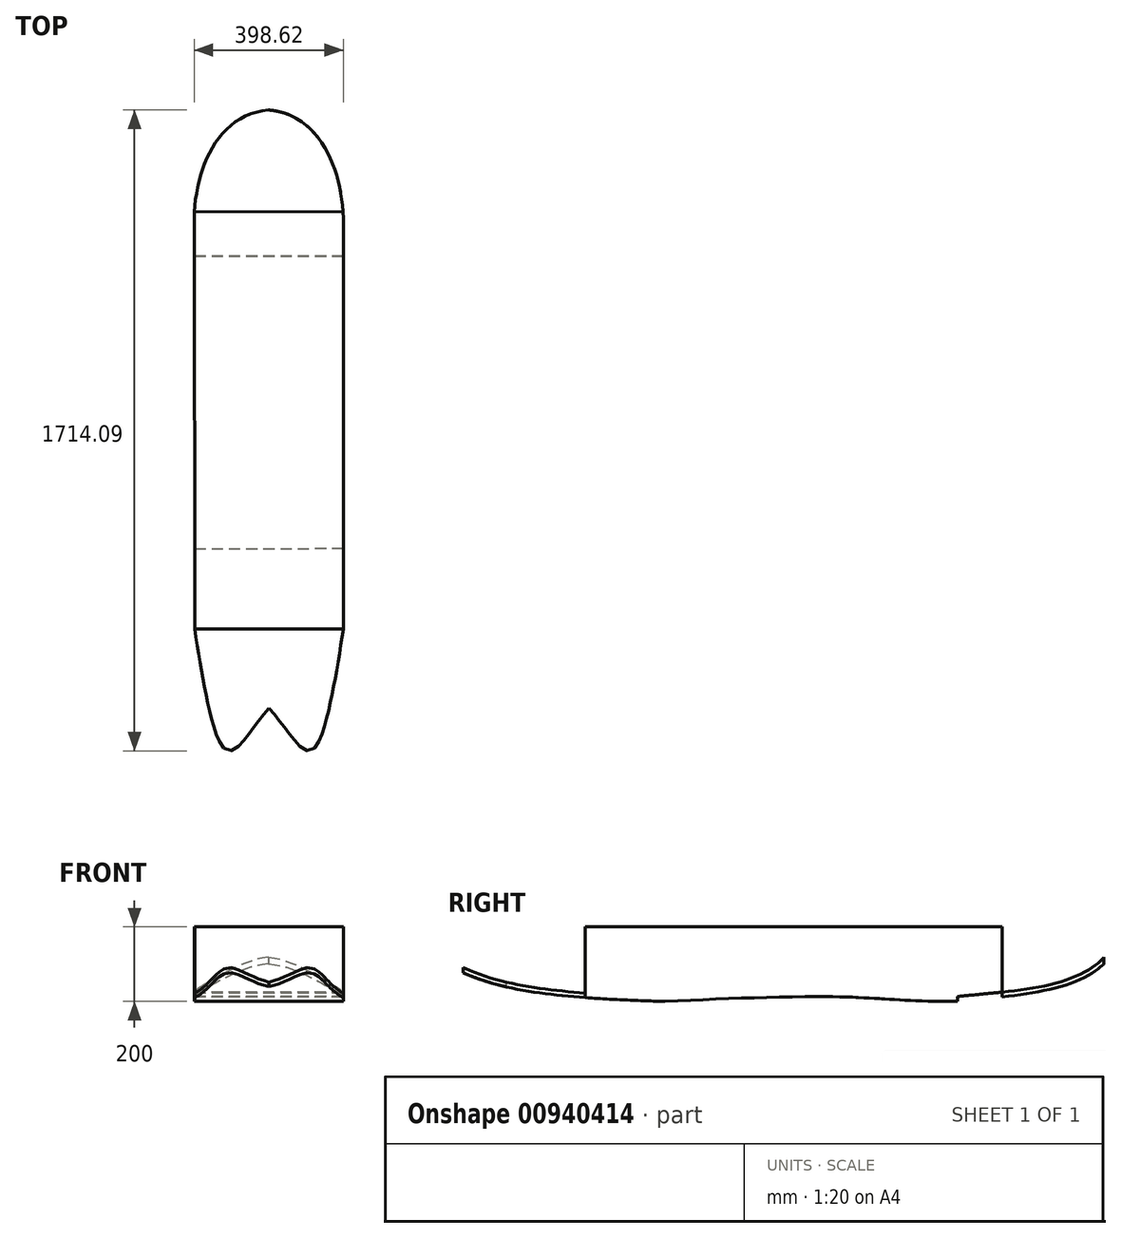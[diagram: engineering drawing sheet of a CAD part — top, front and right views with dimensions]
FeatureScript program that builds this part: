
annotation { "Feature Type Name" : "Feature", "Feature Type Description" : "" }
export const myFeature = defineFeature(function(context is Context, id is Id, definition is map)
    precondition{}
    {
        {
            var Q0;
            Q0=qCreatedBy(makeId("Top.planeOp"),FACE);
            var sketch = newSketch(context, id + "F0", { "sketchPlane" : qUnion([Q0])});
            skLineSegment(sketch, "E0.left", {"start": v(-458, 373.34) * mm, "end": v(-457.07, -741.98) * mm});
            skLineSegment(sketch, "E1", {"start": v(-59.37, 345.67) * mm, "end": v(-59.37, -741.64) * mm});
            skFitSpline(sketch, "E2", {"points": [v(-457.07, -741.98) * mm, v(-258.04, -954.32) * mm], "startDerivative": vector(217.09, -1415.31) * mm, "endDerivative": vector(304.73, 341.04) * mm});
            skFitSpline(sketch, "E3.MirrorCS", {"points": [v(-59.37, -741.64) * mm, v(-258.04, -954.32) * mm], "startDerivative": vector(-214.74, -1415.67) * mm, "endDerivative": vector(-305.3, 340.54) * mm});
            skPoint(sketch, "E4.start.orphan", {"position": v(-458.87, 345.34) * mm});
            skFitSpline(sketch, "E5", {"points": [v(-59.37, 345.67) * mm, v(-259.37, 645.67) * mm], "startDerivative": vector(0, 349.34) * mm, "endDerivative": vector(-450.26, 39.9) * mm});
            skFitSpline(sketch, "E6.MirrorCS", {"points": [v(-458.87, 345.34) * mm, v(-259.37, 645.67) * mm], "startDerivative": vector(-0.58, 349.34) * mm, "endDerivative": vector(450.19, 40.65) * mm});
            skSolve(sketch);
        }
        {
            var Q0;
            {var subQ0=sQuery(id+"F0.wireOp",EDGE,"E0.left");Q0=makeQuery(id+"F0.imprint","IMPRINT",FACE,{"disambiguationData":[TD([[makeQuery(id+"F0.imprint","IMPRINT",EDGE,{"derivedFrom":subQ0}),1.0]])]});}
            extrude(context, id + "F1", {"entities" : qUnion([Q0]), "depth" : 200 * mm, "offsetDistance" : 25 * mm});
        }
        {
            var Q0;
            Q0=makeQuery(id+"F1.opExtrude","SWEPT_FACE",FACE,{"disambiguationData":[OSD([sQuery(id+"F0.wireOp",EDGE,"E0.left")])]});
            var sketch = newSketch(context, id + "F2", { "sketchPlane" : qUnion([Q0])});
            skFitSpline(sketch, "E7", {"points": [v(-681.48, 147.04) * mm, v(-254.45, 0) * mm], "startDerivative": vector(194.6, -372.95) * mm, "endDerivative": vector(506.76, -56.02) * mm});
            skFitSpline(sketch, "E8", {"points": [v(528.22, 0) * mm, v(1137.29, 115.08) * mm], "startDerivative": vector(1077.26, 31.9) * mm, "endDerivative": vector(361.59, 231.4) * mm});
            skFitSpline(sketch, "E9", {"points": [v(-254.45, 0) * mm, v(528.22, 0) * mm], "startDerivative": vector(782.67, 0) * mm, "endDerivative": vector(1747.54, -87.17) * mm});
            skFitSpline(sketch, "E10.0", {"points": [v(527.83, 13) * mm, v(617.46, 15.65) * mm, v(730.29, 21.2) * mm, v(847.64, 33.2) * mm, v(921.66, 44.87) * mm, v(984.24, 59.53) * mm, v(1038.04, 77.54) * mm, v(1085.8, 99.27) * mm, v(1115.51, 116.58) * mm, v(1130.28, 126.03) * mm]});
            skFitSpline(sketch, "E10.1", {"points": [v(-254.45, 13) * mm, v(-221.96, 13) * mm, v(-167.07, 13.9) * mm, v(-114.13, 16.44) * mm, v(-75.4, 18.82) * mm, v(-37.17, 21.26) * mm, v(3.14, 23.54) * mm, v(51.05, 25.14) * mm, v(105.86, 26.11) * mm, v(190.82, 25.82) * mm, v(330.36, 22.07) * mm, v(456, 16.62) * mm, v(528.86, 12.98) * mm]});
            skFitSpline(sketch, "E10.2", {"points": [v(-669.96, 153.06) * mm, v(-666.2, 145.87) * mm, v(-657.8, 132.39) * mm, v(-642.58, 114.55) * mm, v(-624.86, 98.84) * mm, v(-604.77, 85.06) * mm, v(-582.45, 73.07) * mm, v(-549.97, 59.26) * mm, v(-504.81, 45.75) * mm, v(-445.22, 34.24) * mm, v(-382.1, 26) * mm, v(-317.33, 19.49) * mm, v(-274.25, 15.27) * mm, v(-253.02, 12.92) * mm]});
            skLineSegment(sketch, "E11", {"start": v(-681.48, 147.04) * mm, "end": v(-669.96, 153.06) * mm});
            skLineSegment(sketch, "E12", {"start": v(1130.28, 126.03) * mm, "end": v(1137.29, 115.08) * mm});
            skLineSegment(sketch, "E13", {"start": v(-254.45, 0) * mm, "end": v(-253.74, 13) * mm});
            skLineSegment(sketch, "E14", {"start": v(528.22, 0) * mm, "end": v(528.35, 13) * mm});
            skLineSegment(sketch, "E15", {"start": v(528.22, 0) * mm, "end": v(1130.28, 0) * mm});
            skLineSegment(sketch, "E16", {"start": v(1130.28, 0) * mm, "end": v(1137.29, 108.04) * mm});
            skLineSegment(sketch, "E17", {"start": v(1137.29, 108.04) * mm, "end": v(1130.28, 126.03) * mm});
            skLineSegment(sketch, "E18", {"start": v(1130.28, 126.03) * mm, "end": v(1070.45, 213.44) * mm});
            skLineSegment(sketch, "E19", {"start": v(1070.45, 213.44) * mm, "end": v(-131.55, 229.86) * mm});
            skLineSegment(sketch, "E20", {"start": v(-131.55, 229.86) * mm, "end": v(-629.82, 236.66) * mm});
            skLineSegment(sketch, "E21", {"start": v(-629.82, 236.66) * mm, "end": v(-669.96, 153.06) * mm});
            skLineSegment(sketch, "E22", {"start": v(-254.45, 0) * mm, "end": v(-734.2, 0) * mm});
            skLineSegment(sketch, "E23", {"start": v(-734.2, 0) * mm, "end": v(-681.48, 147.04) * mm});
            skSolve(sketch);
        }
        {
            var Q0;
            {var subQ0=sQuery(id+"F2.wireOp",EDGE,"E23");Q0=makeQuery(id+"F2.imprint","IMPRINT",FACE,{"disambiguationData":[TD([[makeQuery(id+"F2.imprint","IMPRINT",EDGE,{"derivedFrom":subQ0}),-1.0]])]});}
            var Q1;
            {var subQ1=sQuery(id+"F2.wireOp",EDGE,"E10.1");Q1=makeQuery(id+"F2.imprint","IMPRINT",FACE,{"disambiguationData":[TD([[makeQuery(id+"F2.imprint","IMPRINT",EDGE,{"derivedFrom":subQ1}),1.0]])]});}
            var Q2;
            {var subQ0=sQuery(id+"F2.wireOp",EDGE,"E18");Q2=makeQuery(id+"F2.imprint","IMPRINT",FACE,{"disambiguationData":[TD([[makeQuery(id+"F2.imprint","IMPRINT",EDGE,{"derivedFrom":subQ0}),1.0]])]});}
            var Q3;
            {var subQ0=sQuery(id+"F2.wireOp",EDGE,"E16");Q3=makeQuery(id+"F2.imprint","IMPRINT",FACE,{"disambiguationData":[TD([[makeQuery(id+"F2.imprint","IMPRINT",EDGE,{"derivedFrom":subQ0}),1.0]])]});}
            var Q4;
            {var subQ0=sQuery(id+"F2.wireOp",EDGE,"E15");var subQ2=sQuery(id+"F0.wireOp",EDGE,"E0.left");var subQ4=makeQuery(id+"F1.opExtrude","SWEPT_EDGE",EDGE,{"disambiguationData":[OSD([subQ2,sQuery(id+"F0.wireOp",EDGE,"E2")])]});var subQ6=makeQuery(id+"F2.imprint","INTERSECT",VERTEX,{"derivedFrom":[subQ4,subQ0]});Q4=makeQuery(id+"F2.imprint","IMPRINT",FACE,{"disambiguationData":[TD([[makeQuery(id+"F2.imprint","IMPRINT",EDGE,{"disambiguationData":[TD([[subQ6,1.0]])],"derivedFrom":subQ4}),-1.0]])]});}
            var Q5;
            {var subQ0=sQuery(id+"F2.wireOp",EDGE,"E22");var subQ2=sQuery(id+"F0.wireOp",EDGE,"E0.left");var subQ4=makeQuery(id+"F1.opExtrude","SWEPT_EDGE",EDGE,{"disambiguationData":[OSD([subQ2,sQuery(id+"F0.wireOp",EDGE,"E6.MirrorCS")])]});var subQ6=makeQuery(id+"F2.imprint","INTERSECT",VERTEX,{"derivedFrom":[subQ4,subQ0]});Q5=makeQuery(id+"F2.imprint","IMPRINT",FACE,{"disambiguationData":[TD([[makeQuery(id+"F2.imprint","IMPRINT",EDGE,{"disambiguationData":[TD([[subQ6,1.0]])],"derivedFrom":subQ4}),1.0]])]});}
            var Q6;
            {var subQ0=sQuery(id+"F2.wireOp",EDGE,"E9");Q6=makeQuery(id+"F2.imprint","IMPRINT",FACE,{"disambiguationData":[TD([[makeQuery(id+"F2.imprint","IMPRINT",EDGE,{"derivedFrom":subQ0}),-1.0]])]});}
            extrude(context, id + "F3", {"entities" : qUnion([Q0, Q1, Q2, Q3, Q4, Q5, Q6]), "operationType" : NewBodyOperationType.REMOVE, "oppositeDirection" : true, "depth" : 400 * mm, "offsetDistance" : 25 * mm});
        }
    });
